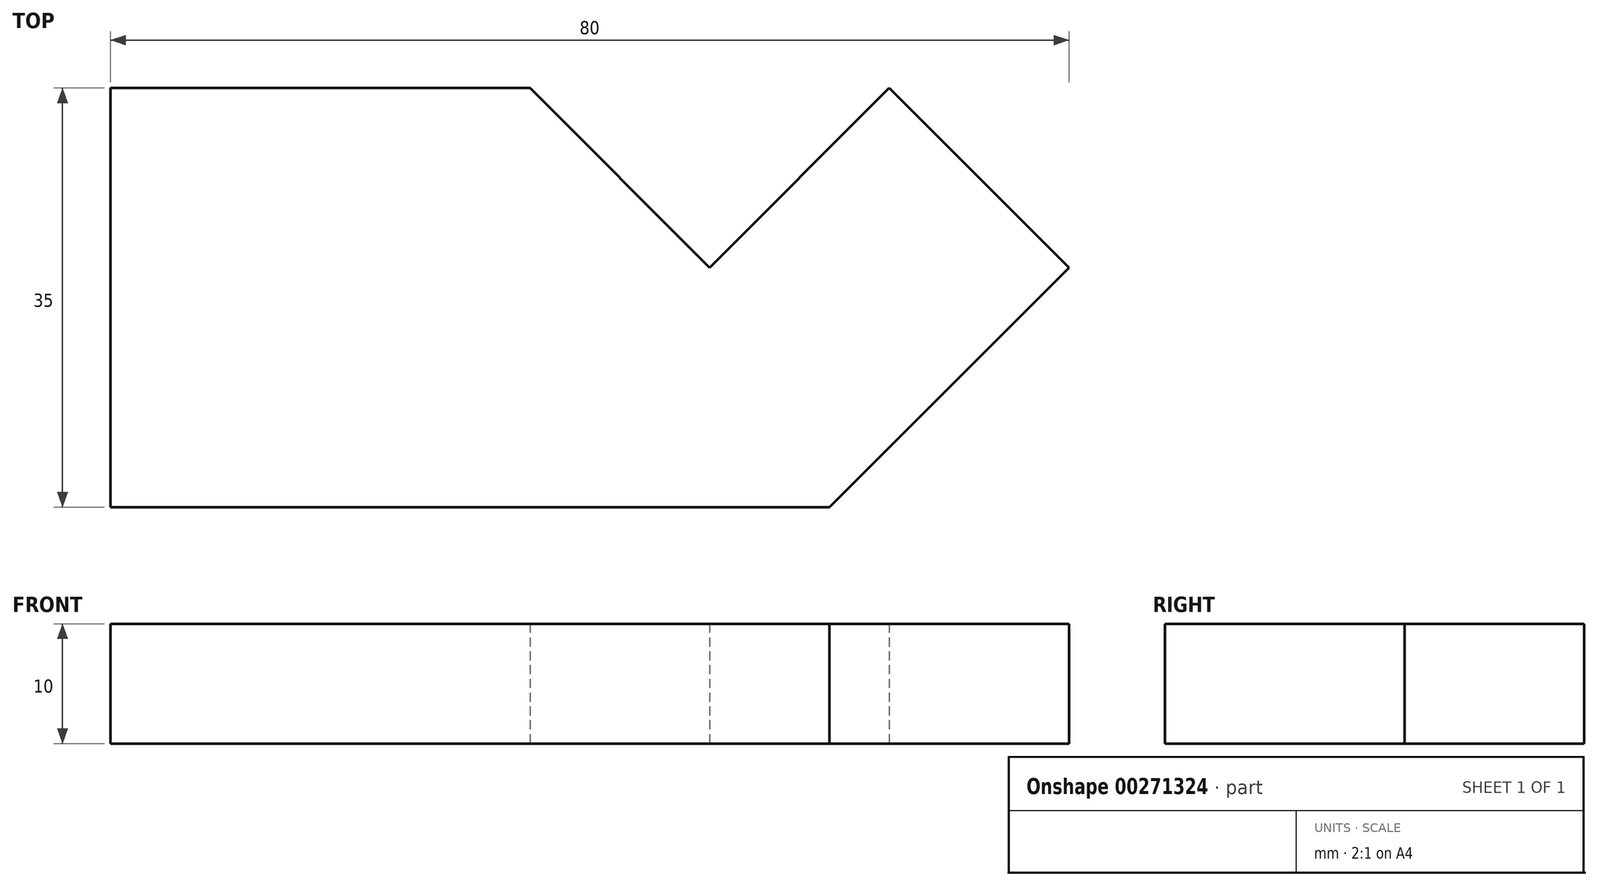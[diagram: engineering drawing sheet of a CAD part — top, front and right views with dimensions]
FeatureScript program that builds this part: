
annotation { "Feature Type Name" : "Feature", "Feature Type Description" : "" }
export const myFeature = defineFeature(function(context is Context, id is Id, definition is map)
    precondition{}
    {
        {
            var Q0;
            Q0=qCreatedBy(makeId("Top.planeOp"),FACE);
            var sketch = newSketch(context, id + "F0", { "sketchPlane" : qUnion([Q0])});
            skLineSegment(sketch, "E0", {"start": v(0, 0) * mm, "end": v(0, 35) * mm});
            skLineSegment(sketch, "E1", {"start": v(0, 35) * mm, "end": v(35, 35) * mm});
            skLineSegment(sketch, "E2", {"start": v(35, 35) * mm, "end": v(50, 20) * mm});
            skLineSegment(sketch, "E3", {"start": v(50, 20) * mm, "end": v(65, 35) * mm});
            skLineSegment(sketch, "E4", {"start": v(65, 35) * mm, "end": v(80, 20) * mm});
            skLineSegment(sketch, "E5", {"start": v(80, 20) * mm, "end": v(60, 0) * mm});
            skLineSegment(sketch, "E6", {"start": v(60, 0) * mm, "end": v(0, 0) * mm});
            skSolve(sketch);
        }
        {
            var Q0;
            Q0 = qSketchRegion(id + "F0", true);
            extrude(context, id + "F1", {"entities" : qUnion([Q0]), "depth" : 10 * mm});
        }
    });
